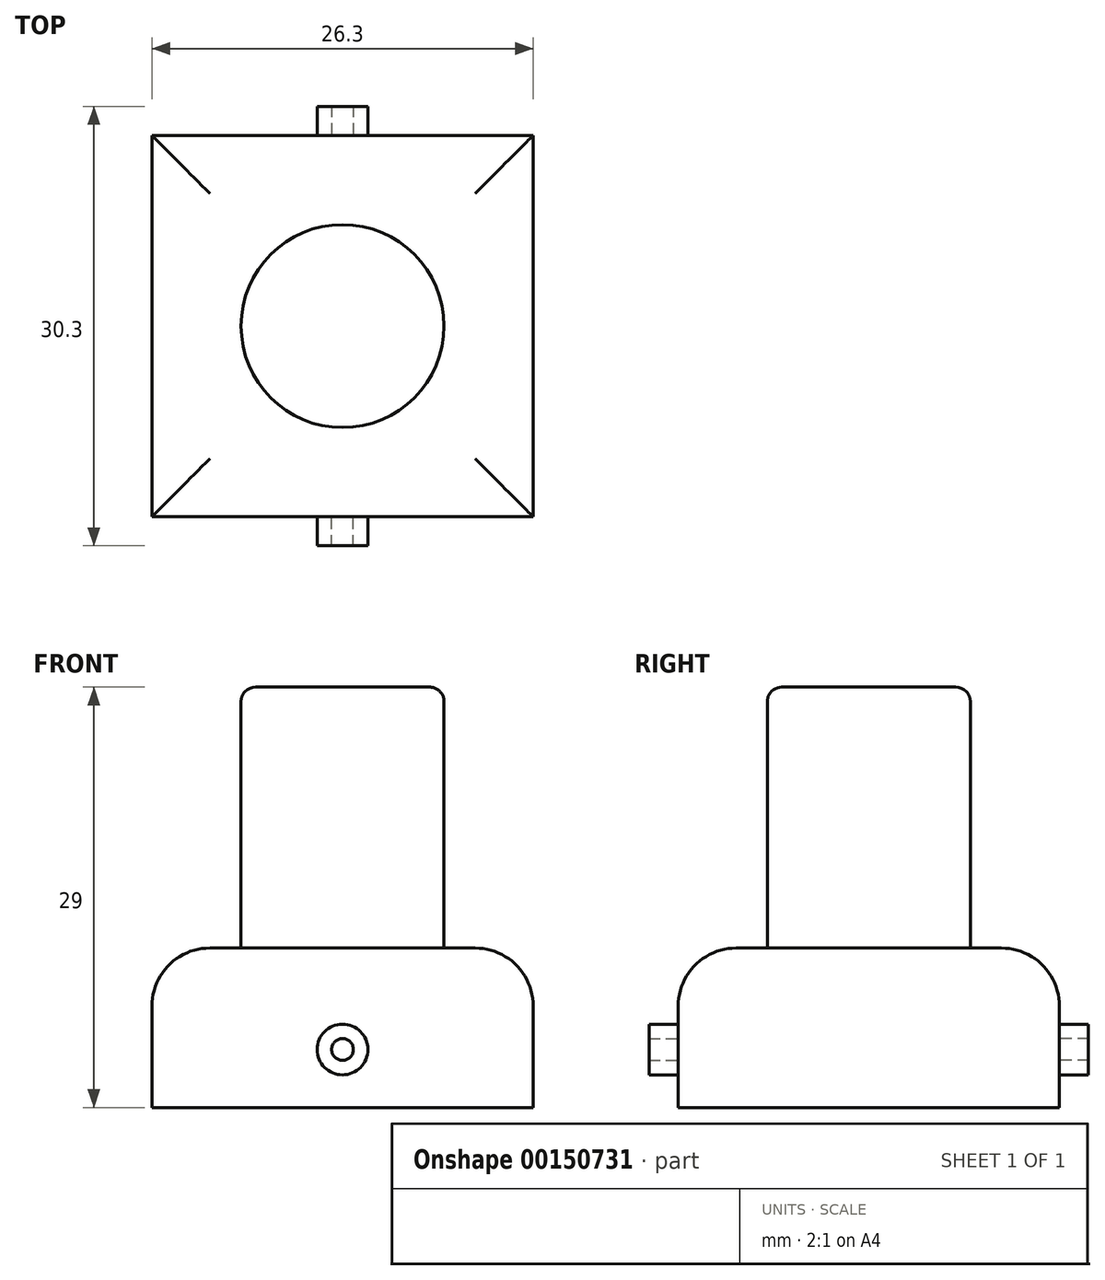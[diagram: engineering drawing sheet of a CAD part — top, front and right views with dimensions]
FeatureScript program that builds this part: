
annotation { "Feature Type Name" : "Feature", "Feature Type Description" : "" }
export const myFeature = defineFeature(function(context is Context, id is Id, definition is map)
    precondition{}
    {
        {
            var Q0;
            Q0=qCreatedBy(makeId("Top.planeOp"),FACE);
            var sketch = newSketch(context, id + "F0", { "sketchPlane" : qUnion([Q0])});
            skLineSegment(sketch, "E0.bottom", {"start": v(0, 0) * mm, "end": v(26.3, 0) * mm});
            skLineSegment(sketch, "E0.top", {"start": v(0, -26.3) * mm, "end": v(26.3, -26.3) * mm});
            skLineSegment(sketch, "E0.left", {"start": v(0, 0) * mm, "end": v(0, -26.3) * mm});
            skLineSegment(sketch, "E0.right", {"start": v(26.3, 0) * mm, "end": v(26.3, -26.3) * mm});
            skSolve(sketch);
        }
        {
            var Q0;
            Q0=makeQuery(id+"F0.imprint","IMPRINT",FACE,{"disambiguationData":[TD([[makeQuery(id+"F0.imprint","IMPRINT",EDGE,{"derivedFrom":sQuery(id+"F0.wireOp",EDGE,"E0.bottom")}),-1.0]])]});
            extrude(context, id + "F1", {"entities" : qUnion([Q0]), "depth" : 11 * mm});
        }
        {
            var Q0;
            Q0=makeQuery(id+"F1.opExtrude","CAP_EDGE",EDGE,{"disambiguationData":[OSD([sQuery(id+"F0.wireOp",EDGE,"E0.top")])],"isStart":false});
            var Q1;
            Q1=makeQuery(id+"F1.opExtrude","CAP_EDGE",EDGE,{"disambiguationData":[OSD([sQuery(id+"F0.wireOp",EDGE,"E0.left")])],"isStart":false});
            var Q2;
            Q2=makeQuery(id+"F1.opExtrude","CAP_EDGE",EDGE,{"disambiguationData":[OSD([sQuery(id+"F0.wireOp",EDGE,"E0.right")])],"isStart":false});
            var Q3;
            Q3=makeQuery(id+"F1.opExtrude","CAP_EDGE",EDGE,{"disambiguationData":[OSD([sQuery(id+"F0.wireOp",EDGE,"E0.bottom")])],"isStart":false});
            fillet(context, id + "F2", {"entities" : qUnion([Q0, Q1, Q2, Q3]), "radius" : 4 * mm, "tangentPropagation" : true, "allowEdgeOverflow" : false});
        }
        {
            var Q0;
            Q0=makeQuery(id+"F1.opExtrude","CAP_FACE",FACE,{"disambiguationData":[OSD([sQuery(id+"F0.wireOp",EDGE,"E0.bottom"),sQuery(id+"F0.wireOp",EDGE,"E0.top"),sQuery(id+"F0.wireOp",EDGE,"E0.left"),sQuery(id+"F0.wireOp",EDGE,"E0.right")])],"isStart":false});
            var sketch = newSketch(context, id + "F3", { "sketchPlane" : qUnion([Q0])});
            skLineSegment(sketch, "E1", {"start": v(13.15, -7.1) * mm, "end": v(13.15, -18.45) * mm, "construction": true});
            skPoint(sketch, "E1.startSnap0", {"position": v(13.15, -4) * mm});
            skLineSegment(sketch, "E2", {"start": v(6.68, -13.15) * mm, "end": v(18.76, -13.15) * mm, "construction": true});
            skPoint(sketch, "E2.startSnap0", {"position": v(4, -13.15) * mm});
            skCircle(sketch, "E3", {"center": v(13.15, -13.15) * mm, "radius": 7 * mm});
            skSolve(sketch);
        }
        {
            var Q0;
            Q0=makeQuery(id+"F3.imprint","IMPRINT",FACE,{"disambiguationData":[TD([[makeQuery(id+"F3.imprint","IMPRINT",EDGE,{"derivedFrom":sQuery(id+"F3.wireOp",EDGE,"E3")}),1.0]])]});
            extrude(context, id + "F4", {"entities" : qUnion([Q0]), "operationType" : NewBodyOperationType.ADD, "depth" : 18 * mm});
        }
        {
            var Q0;
            Q0=makeQuery(id+"F1.opExtrude","SWEPT_FACE",FACE,{"disambiguationData":[OSD([sQuery(id+"F0.wireOp",EDGE,"E0.top")])]});
            var sketch = newSketch(context, id + "F5", { "sketchPlane" : qUnion([Q0])});
            skCircle(sketch, "E4", {"center": v(13.15, 4) * mm, "radius": 1.75 * mm});
            skCircle(sketch, "E5", {"center": v(13.15, 4) * mm, "radius": 0.75 * mm});
            skSolve(sketch);
        }
        {
            var Q0;
            Q0=makeQuery(id+"F5.imprint","IMPRINT",FACE,{"disambiguationData":[TD([[makeQuery(id+"F5.imprint","IMPRINT",EDGE,{"derivedFrom":sQuery(id+"F5.wireOp",EDGE,"E4")}),1.0]])]});
            extrude(context, id + "F6", {"entities" : qUnion([Q0]), "operationType" : NewBodyOperationType.ADD, "depth" : 2 * mm});
        }
        {
            var Q0;
            Q0=makeQuery(id+"F1.opExtrude","SWEPT_FACE",FACE,{"disambiguationData":[OSD([sQuery(id+"F0.wireOp",EDGE,"E0.bottom")])]});
            var sketch = newSketch(context, id + "F7", { "sketchPlane" : qUnion([Q0])});
            skCircle(sketch, "E6", {"center": v(-13.15, 4) * mm, "radius": 1.75 * mm});
            skCircle(sketch, "E7", {"center": v(-13.15, 4) * mm, "radius": 0.75 * mm});
            skSolve(sketch);
        }
        {
            var Q0;
            Q0=makeQuery(id+"F7.imprint","IMPRINT",FACE,{"disambiguationData":[TD([[makeQuery(id+"F7.imprint","IMPRINT",EDGE,{"derivedFrom":sQuery(id+"F7.wireOp",EDGE,"E6")}),1.0]])]});
            extrude(context, id + "F8", {"entities" : qUnion([Q0]), "operationType" : NewBodyOperationType.ADD, "depth" : 2 * mm});
        }
        {
            var Q0;
            Q0=makeQuery(id+"F4.opExtrude","CAP_EDGE",EDGE,{"disambiguationData":[OSD([sQuery(id+"F3.wireOp",EDGE,"E3")])],"isStart":false});
            fillet(context, id + "F9", {"entities" : qUnion([Q0]), "radius" : 1 * mm, "tangentPropagation" : true, "allowEdgeOverflow" : false});
        }
    });
